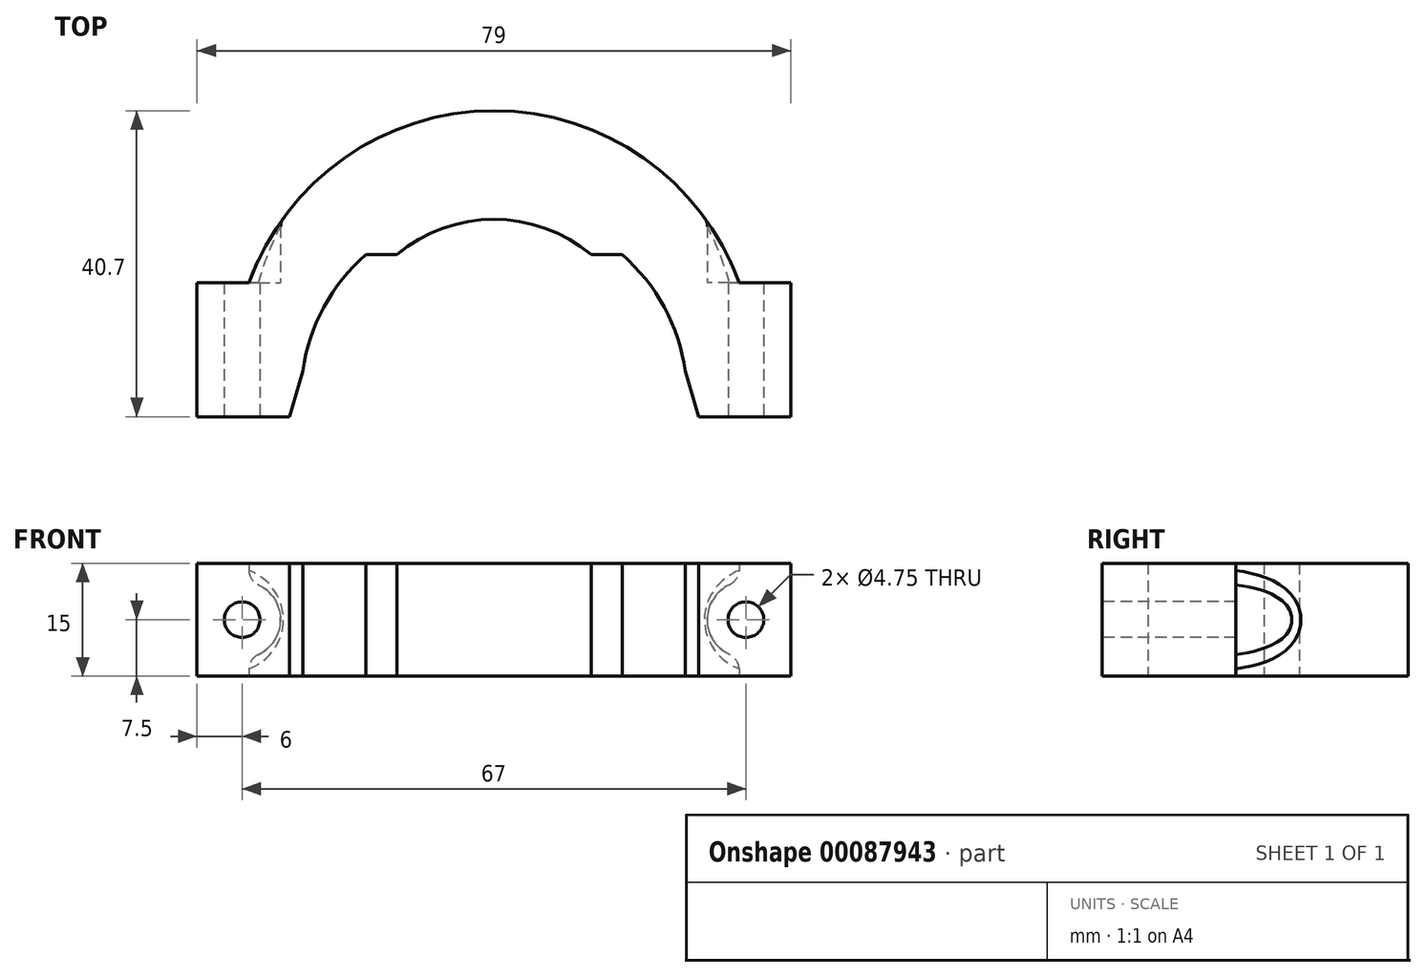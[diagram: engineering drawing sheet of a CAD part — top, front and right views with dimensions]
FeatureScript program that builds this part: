
annotation { "Feature Type Name" : "Feature", "Feature Type Description" : "" }
export const myFeature = defineFeature(function(context is Context, id is Id, definition is map)
    precondition{}
    {
        {
            var Q0;
            Q0=qCreatedBy(makeId("Top.planeOp"),FACE);
            var sketch = newSketch(context, id + "F0", { "sketchPlane" : qUnion([Q0])});
            skLineSegment(sketch, "E0", {"start": v(12.94, 0) * mm, "end": v(17.04, 0) * mm});
            skArc(sketch, "E1", {"start": v(12.94, 0) * mm, "mid": v(6.88, 3.48) * mm, "end": v(0, 4.69) * mm});
            skArc(sketch, "E2", {"start": v(25.42, -15.47) * mm, "mid": v(22.64, -6.97) * mm, "end": v(17.04, 0) * mm});
            skLineSegment(sketch, "E3", {"start": v(25.42, -15.47) * mm, "end": v(27.2, -21.56) * mm});
            skLineSegment(sketch, "E4", {"start": v(27.2, -21.56) * mm, "end": v(39.5, -21.56) * mm});
            skLineSegment(sketch, "E5", {"start": v(39.5, -21.56) * mm, "end": v(39.5, -3.76) * mm});
            skLineSegment(sketch, "E6", {"start": v(39.5, -3.76) * mm, "end": v(32.6, -3.76) * mm});
            skArc(sketch, "E7", {"start": v(32.6, -3.76) * mm, "mid": v(19.92, 12.84) * mm, "end": v(0, 19.14) * mm});
            skLineSegment(sketch, "E8", {"start": v(0, 4.69) * mm, "end": v(0, 19.14) * mm, "construction": true});
            skPoint(sketch, "E9.orphan", {"position": v(-12.94, 0) * mm});
            skLineSegment(sketch, "E10.MirrorCS", {"start": v(-25.42, -15.47) * mm, "end": v(-27.2, -21.56) * mm});
            skLineSegment(sketch, "E11.MirrorCS", {"start": v(-12.94, 0) * mm, "end": v(-17.04, 0) * mm});
            skLineSegment(sketch, "E12.MirrorCS", {"start": v(-27.2, -21.56) * mm, "end": v(-39.5, -21.56) * mm});
            skArc(sketch, "E13.MirrorCS", {"start": v(-32.6, -3.76) * mm, "mid": v(-19.92, 12.84) * mm, "end": v(0, 19.14) * mm});
            skLineSegment(sketch, "E14.MirrorCS", {"start": v(-39.5, -3.76) * mm, "end": v(-32.6, -3.76) * mm});
            skLineSegment(sketch, "E15.MirrorCS", {"start": v(-39.5, -21.56) * mm, "end": v(-39.5, -3.76) * mm});
            skArc(sketch, "E16.MirrorCS", {"start": v(-25.42, -15.47) * mm, "mid": v(-22.64, -6.97) * mm, "end": v(-17.04, 0) * mm});
            skArc(sketch, "E17.MirrorCS", {"start": v(-12.94, 0) * mm, "mid": v(-6.88, 3.48) * mm, "end": v(0, 4.69) * mm});
            skPoint(sketch, "E18.MirrorP", {"position": v(12.94, 0) * mm});
            skSolve(sketch);
        }
        {
            var Q0;
            Q0=makeQuery(id+"F0.imprint","IMPRINT",FACE,{"disambiguationData":[TD([[makeQuery(id+"F0.imprint","IMPRINT",EDGE,{"derivedFrom":sQuery(id+"F0.wireOp",EDGE,"E0")}),1.0]])]});
            extrude(context, id + "F1", {"entities" : qUnion([Q0]), "depth" : 15 * mm});
        }
        {
            var Q0;
            Q0=makeQuery(id+"F1.opExtrude","SWEPT_FACE",FACE,{"disambiguationData":[OSD([sQuery(id+"F0.wireOp",EDGE,"E12.MirrorCS")])]});
            var sketch = newSketch(context, id + "F2", { "sketchPlane" : qUnion([Q0])});
            skLineSegment(sketch, "E19", {"start": v(-31.13, 7.5) * mm, "end": v(31.13, 7.5) * mm, "construction": true});
            skCircle(sketch, "E20", {"center": v(-33.5, 7.5) * mm, "radius": 2.38 * mm});
            skCircle(sketch, "E21", {"center": v(33.5, 7.5) * mm, "radius": 2.38 * mm});
            skLineSegment(sketch, "E22", {"start": v(0, 0) * mm, "end": v(0, 7.5) * mm, "construction": true});
            skLineSegment(sketch, "E23", {"start": v(33.5, 7.5) * mm, "end": v(39.5, 7.5) * mm, "construction": true});
            skSolve(sketch);
        }
        {
            var Q0;
            Q0=makeQuery(id+"F2.imprint","IMPRINT",FACE,{"disambiguationData":[TD([[makeQuery(id+"F2.imprint","IMPRINT",EDGE,{"derivedFrom":sQuery(id+"F2.wireOp",EDGE,"E20")}),1.0]])]});
            var Q1;
            Q1=makeQuery(id+"F2.imprint","IMPRINT",FACE,{"disambiguationData":[TD([[makeQuery(id+"F2.imprint","IMPRINT",EDGE,{"derivedFrom":sQuery(id+"F2.wireOp",EDGE,"E21")}),1.0]])]});
            extrude(context, id + "F3", {"entities" : qUnion([Q0, Q1]), "operationType" : NewBodyOperationType.REMOVE, "oppositeDirection" : true, "depth" : 25 * mm});
        }
        {
            var Q0;
            Q0=makeQuery(id+"F1.opExtrude","SWEPT_FACE",FACE,{"disambiguationData":[OSD([sQuery(id+"F0.wireOp",EDGE,"E14.MirrorCS")])]});
            var sketch = newSketch(context, id + "F4", { "sketchPlane" : qUnion([Q0])});
            skCircle(sketch, "E24", {"center": v(33.5, 7.5) * mm, "radius": 5.12 * mm});
            skCircle(sketch, "E25", {"center": v(-33.5, 7.5) * mm, "radius": 5.12 * mm});
            skSolve(sketch);
        }
        {
            var Q0;
            Q0 = qSketchRegion(id + "F4", true);
            extrude(context, id + "F5", {"entities" : qUnion([Q0]), "operationType" : NewBodyOperationType.REMOVE, "depth" : 25 * mm});
        }
        {
            var Q0;
            Q0=makeQuery(id+"F5.boolean.opBoolean","INTERSECT",EDGE,{"derivedFrom":[makeQuery(id+"F1.opExtrude","SWEPT_FACE",FACE,{"disambiguationData":[OSD([sQuery(id+"F0.wireOp",EDGE,"E7"),sQuery(id+"F0.wireOp",EDGE,"E13.MirrorCS")])]}),makeQuery(id+"F5.opExtrude","SWEPT_FACE",FACE,{"disambiguationData":[OSD([sQuery(id+"F4.wireOp",EDGE,"E25")])]})]});
            var Q1;
            Q1=makeQuery(id+"F5.boolean.opBoolean","INTERSECT",EDGE,{"derivedFrom":[makeQuery(id+"F1.opExtrude","SWEPT_FACE",FACE,{"disambiguationData":[OSD([sQuery(id+"F0.wireOp",EDGE,"E7"),sQuery(id+"F0.wireOp",EDGE,"E13.MirrorCS")])]}),makeQuery(id+"F5.opExtrude","SWEPT_FACE",FACE,{"disambiguationData":[OSD([sQuery(id+"F4.wireOp",EDGE,"E24")])]})]});
            fillet(context, id + "F6", {"entities" : qUnion([Q0, Q1]), "radius" : 2 * mm, "tangentPropagation" : true, "allowEdgeOverflow" : false});
        }
    });
